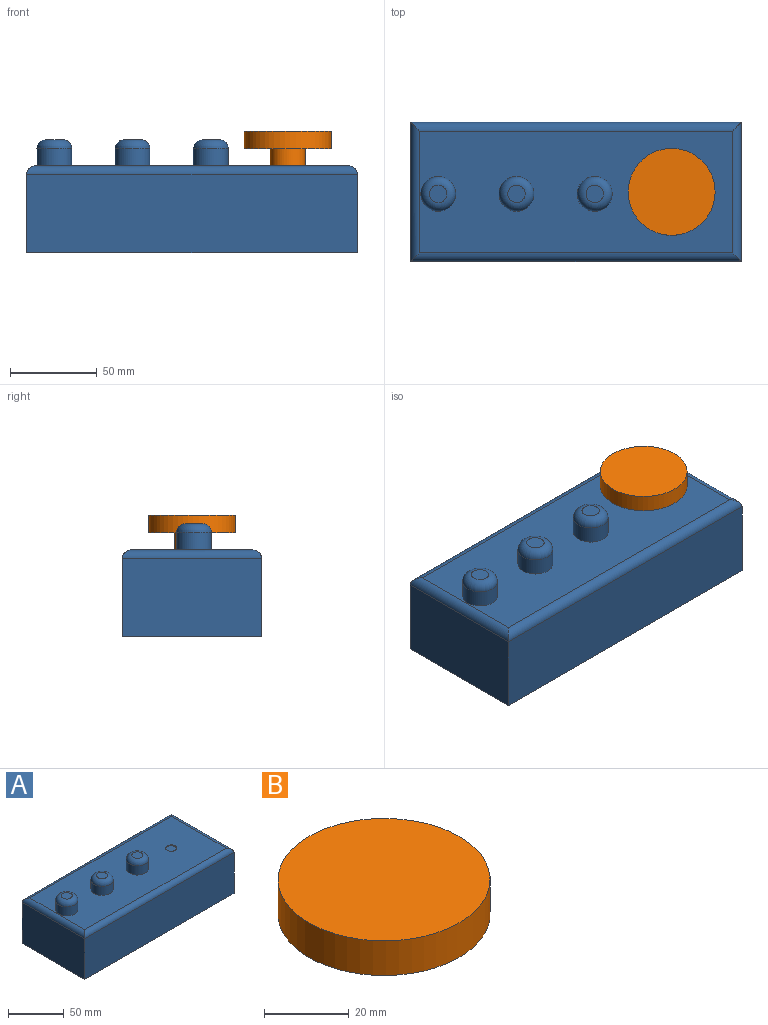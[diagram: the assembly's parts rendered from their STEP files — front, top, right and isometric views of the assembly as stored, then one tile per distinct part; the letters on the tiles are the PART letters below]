
ASSEMBLY  parts=2 mates=2
PART A: 21 faces, bbox 190x80x65 mm
  f0: plane 80x45mm, normal (-1,0,0), area 3600mm2, adj f1,f3,f5,f17
  f1: plane 190x45mm, normal (0,-1,0), area 8550mm2, adj f0,f2,f5,f19
  f2: plane 80x45mm, normal (1,0,0), area 3600mm2, adj f1,f3,f5,f20
  f3: plane 190x45mm, normal (0,1,0), area 8550mm2, adj f0,f2,f5,f18
  f4: plane 180x70mm, normal (0,0,1), area 11579mm2, adj f6,f8,f10,f12,f17,f18,f19,f20
  f5: plane 190x80mm, normal (0,0,-1), area 15200mm2, adj f0,f1,f2,f3
  f6: cylinder r=5mm len=10mm, axis (0,0,1), area 31.4mm2, adj f4,f7
  f7: plane 10x10mm, normal (0,0,1), area 78.5mm2, adj f6
  f8: cylinder r=10mm len=20mm, axis (0,0,-1), area 628.3mm2, adj f4,f15
  f9: plane 10x10mm, normal (0,0,1), area 78.5mm2, adj f15
  f10: cylinder r=10mm len=20mm, axis (0,0,-1), area 628.3mm2, adj f4,f14
  f11: plane 10x10mm, normal (0,0,1), area 78.5mm2, adj f14
  f12: cylinder r=10mm len=20mm, axis (0,0,-1), area 628.3mm2, adj f4,f16
  f13: plane 10x10mm, normal (0,0,1), area 78.5mm2, adj f16
  f14: torus R=5mm, axis (0,0,1), area 403.8mm2, adj f10,f11
  f15: torus R=5mm, axis (0,0,1), area 403.8mm2, adj f8,f9
  f16: torus R=5mm, axis (0,0,1), area 403.8mm2, adj f12,f13
  f17: cylinder r=5mm len=80mm, axis (0,1,0), area 599.8mm2, adj f0,f4,f18,f19
  f18: cylinder r=5mm len=190mm, axis (1,0,0), area 1463.7mm2, adj f3,f4,f17,f20
  f19: cylinder r=5mm len=190mm, axis (-1,0,0), area 1463.7mm2, adj f1,f4,f17,f20
  f20: cylinder r=5mm len=80mm, axis (0,-1,0), area 599.8mm2, adj f2,f4,f18,f19
PART B: 5 faces, bbox 50x50x20 mm
  f0: cylinder r=10mm len=20mm, axis (0,0,-1), area 628.3mm2, adj f1,f4
  f1: plane 20x20mm, normal (0,0,-1), area 314.2mm2, adj f0
  f2: cylinder r=25mm len=50mm, axis (0,0,-1), area 1570.8mm2, adj f3,f4
  f3: plane 50x50mm, normal (0,0,1), area 1963.5mm2, adj f2
  f4: plane 50x50mm, normal (0,0,-1), area 1649.3mm2, adj f0,f2
PLACE A t=(-175.98,27.81,-12.92)mm
PLACE B rot(axis=(0,0,1),90deg) t=(-25.98,-12.19,37.08)mm
MATE planar B.f0 <-> A.f4  axis (0,0,-1) through (-25.98,-12.19,37.08)mm
MATE revolute B.f0 <-> A.f6  axis (0,0,-1) through (-25.98,-12.19,37.08)mm
